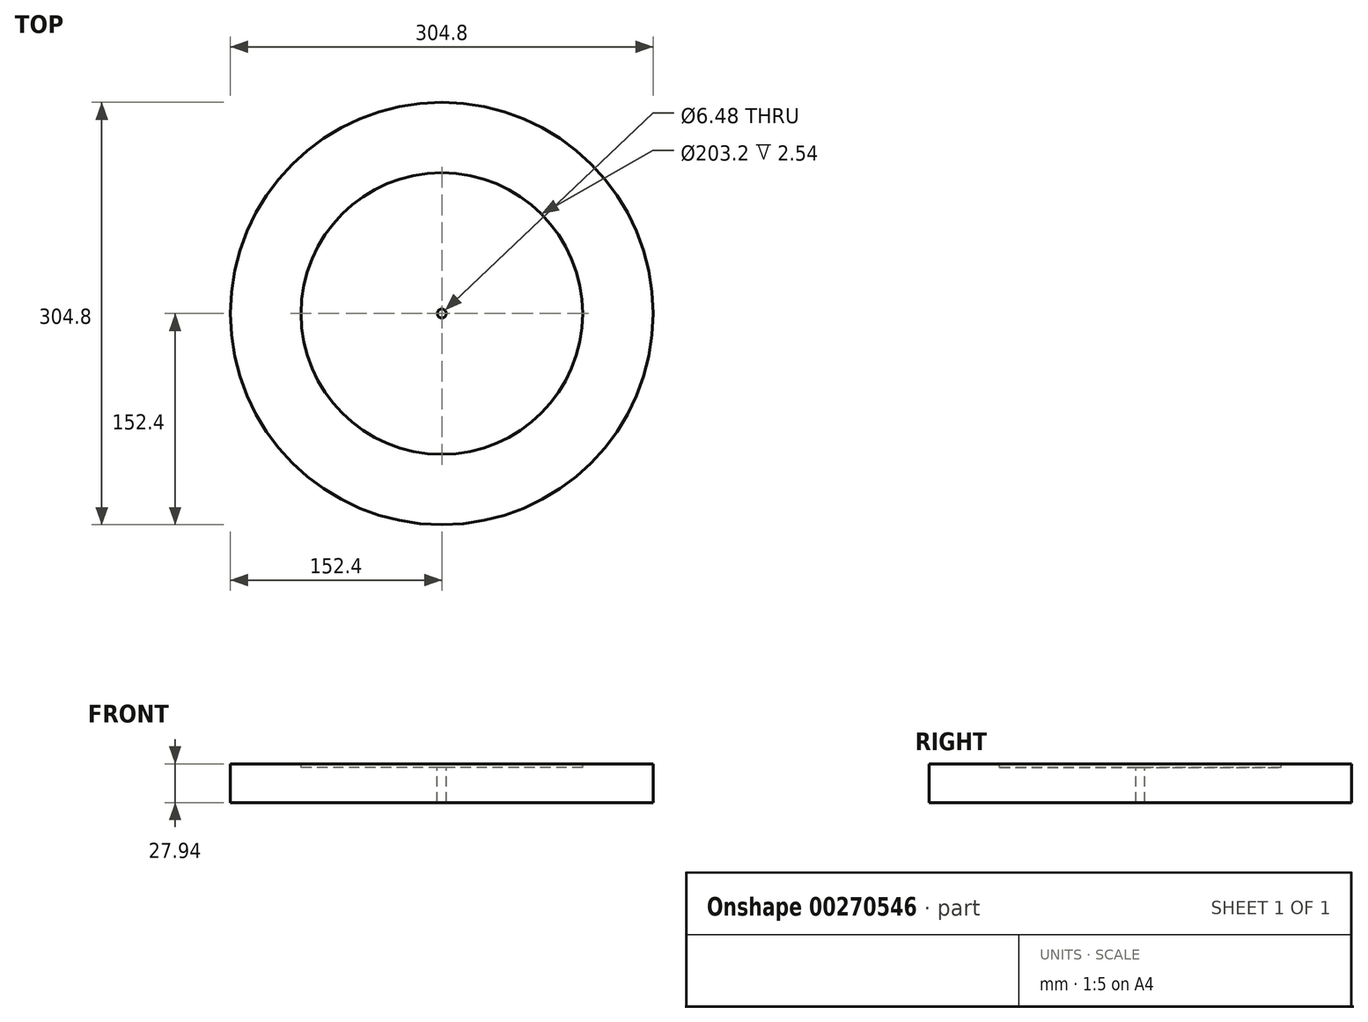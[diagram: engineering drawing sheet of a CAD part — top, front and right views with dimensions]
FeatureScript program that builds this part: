
annotation { "Feature Type Name" : "Feature", "Feature Type Description" : "" }
export const myFeature = defineFeature(function(context is Context, id is Id, definition is map)
    precondition{}
    {
        {
            var Q0;
            Q0=qCreatedBy(makeId("Top.planeOp"),FACE);
            var sketch = newSketch(context, id + "F0", { "sketchPlane" : qUnion([Q0])});
            skCircle(sketch, "E0", {"center": v(0, 0) * mm, "radius": 152.4 * mm});
            skSolve(sketch);
        }
        {
            var Q0;
            Q0=makeQuery(id+"F0.imprint","IMPRINT",FACE,{"disambiguationData":[TD([[makeQuery(id+"F0.imprint","IMPRINT",EDGE,{"derivedFrom":sQuery(id+"F0.wireOp",EDGE,"E0")}),1.0]])]});
            extrude(context, id + "F1", {"entities" : qUnion([Q0]), "depth" : 27.94 * mm});
        }
        {
            var Q0;
            Q0=makeQuery(id+"F1.opExtrude","CAP_FACE",FACE,{"disambiguationData":[OSD([sQuery(id+"F0.wireOp",EDGE,"E0")])],"isStart":false});
            var sketch = newSketch(context, id + "F2", { "sketchPlane" : qUnion([Q0])});
            skCircle(sketch, "E1", {"center": v(0, 0) * mm, "radius": 3.24 * mm});
            skSolve(sketch);
        }
        {
            var Q0;
            Q0 = qSketchRegion(id + "F2", true);
            var Q1;
            Q1=makeQuery(id+"F1.opExtrude","CAP_FACE",FACE,{"disambiguationData":[OSD([sQuery(id+"F0.wireOp",EDGE,"E0")])],"isStart":true});
            extrude(context, id + "F3", {"entities" : qUnion([Q0]), "operationType" : NewBodyOperationType.REMOVE, "endBound" : BoundingType.UP_TO_SURFACE, "oppositeDirection" : true, "endBoundEntityFace" : qUnion([Q1]), "depth" : 25.4 * mm});
        }
        {
            var Q0;
            Q0=makeQuery(id+"F1.opExtrude","CAP_FACE",FACE,{"disambiguationData":[OSD([sQuery(id+"F0.wireOp",EDGE,"E0")])],"isStart":false});
            var sketch = newSketch(context, id + "F4", { "sketchPlane" : qUnion([Q0])});
            skSolve(sketch);
        }
        {
            var Q0;
            Q0=makeQuery(id+"F4.imprint","IMPRINT",FACE,{"disambiguationData":[TD([[makeQuery(id+"F4.imprint","IMPRINT",EDGE,{"derivedFrom":makeQuery(id+"F1.opExtrude","CAP_EDGE",EDGE,{"disambiguationData":[OSD([sQuery(id+"F0.wireOp",EDGE,"E0")])],"isStart":false})}),1.0]])]});
            var sketch = newSketch(context, id + "F5", { "sketchPlane" : qUnion([Q0])});
            skCircle(sketch, "E2", {"center": v(0, 0) * mm, "radius": 101.6 * mm});
            skSolve(sketch);
        }
        {
            var Q0;
            Q0 = qSketchRegion(id + "F5", true);
            extrude(context, id + "F6", {"entities" : qUnion([Q0]), "operationType" : NewBodyOperationType.REMOVE, "oppositeDirection" : true, "depth" : 2.54 * mm});
        }
    });
